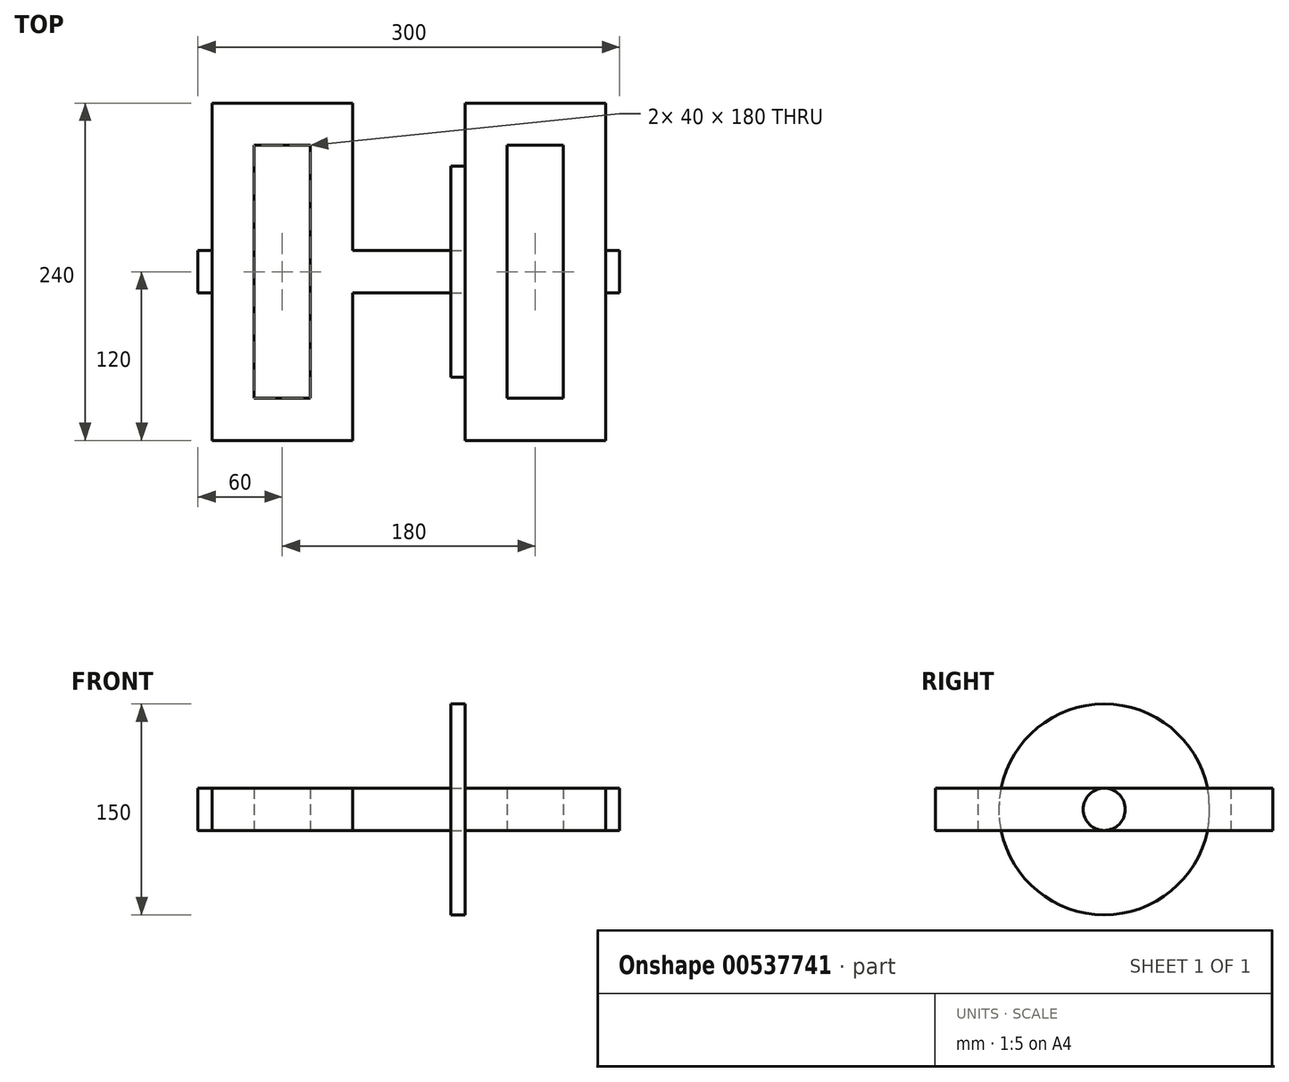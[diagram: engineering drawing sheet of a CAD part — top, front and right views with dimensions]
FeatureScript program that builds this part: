
annotation { "Feature Type Name" : "Feature", "Feature Type Description" : "" }
export const myFeature = defineFeature(function(context is Context, id is Id, definition is map)
    precondition{}
    {
        {
            var Q0;
            Q0=qCreatedBy(makeId("Top.planeOp"),FACE);
            var sketch = newSketch(context, id + "F0", { "sketchPlane" : qUnion([Q0])});
            skLineSegment(sketch, "E0.bottom", {"start": v(-150, 15) * mm, "end": v(-140, 15) * mm});
            skLineSegment(sketch, "E0.top", {"start": v(-150, -15) * mm, "end": v(-140, -15) * mm});
            skLineSegment(sketch, "E0.left", {"start": v(-150, 15) * mm, "end": v(-150, -15) * mm});
            skLineSegment(sketch, "E0.right", {"start": v(-140, 15) * mm, "end": v(-140, -15) * mm});
            skLineSegment(sketch, "E1.bottom", {"start": v(-140, 120) * mm, "end": v(-40, 120) * mm});
            skLineSegment(sketch, "E1.top", {"start": v(-140, -120) * mm, "end": v(-40, -120) * mm});
            skLineSegment(sketch, "E1.left", {"start": v(-140, 120) * mm, "end": v(-140, -120) * mm});
            skLineSegment(sketch, "E1.right", {"start": v(-40, 120) * mm, "end": v(-40, -120) * mm});
            skLineSegment(sketch, "E2.bottom", {"start": v(-40, 15) * mm, "end": v(40, 15) * mm});
            skLineSegment(sketch, "E2.top", {"start": v(-40, -15) * mm, "end": v(40, -15) * mm});
            skLineSegment(sketch, "E2.left", {"start": v(-40, 15) * mm, "end": v(-40, -15) * mm});
            skLineSegment(sketch, "E2.right", {"start": v(40, 15) * mm, "end": v(40, -15) * mm});
            skLineSegment(sketch, "E3.bottom", {"start": v(40, 120) * mm, "end": v(140, 120) * mm});
            skLineSegment(sketch, "E3.top", {"start": v(40, -120) * mm, "end": v(140, -120) * mm});
            skLineSegment(sketch, "E3.left", {"start": v(40, 120) * mm, "end": v(40, -120) * mm});
            skLineSegment(sketch, "E3.right", {"start": v(140, 120) * mm, "end": v(140, -120) * mm});
            skLineSegment(sketch, "E4.bottom", {"start": v(140, 15) * mm, "end": v(150, 15) * mm});
            skLineSegment(sketch, "E4.top", {"start": v(140, -15) * mm, "end": v(150, -15) * mm});
            skLineSegment(sketch, "E4.left", {"start": v(140, 15) * mm, "end": v(140, -15) * mm});
            skLineSegment(sketch, "E4.right", {"start": v(150, 15) * mm, "end": v(150, -15) * mm});
            skLineSegment(sketch, "E5.bottom", {"start": v(-110, 90) * mm, "end": v(-70, 90) * mm});
            skLineSegment(sketch, "E5.top", {"start": v(-110, -90) * mm, "end": v(-70, -90) * mm});
            skLineSegment(sketch, "E5.left", {"start": v(-110, 90) * mm, "end": v(-110, -90) * mm});
            skLineSegment(sketch, "E5.right", {"start": v(-70, 90) * mm, "end": v(-70, -90) * mm});
            skPoint(sketch, "E6.oppositeSnap0", {"position": v(-90, -90) * mm});
            skLineSegment(sketch, "E6.bottom", {"start": v(70, 90) * mm, "end": v(110, 90) * mm});
            skLineSegment(sketch, "E6.top", {"start": v(70, -90) * mm, "end": v(110, -90) * mm});
            skLineSegment(sketch, "E6.left", {"start": v(70, 90) * mm, "end": v(70, -90) * mm});
            skLineSegment(sketch, "E6.right", {"start": v(110, 90) * mm, "end": v(110, -90) * mm});
            skSolve(sketch);
        }
        {
            var Q0;
            {var subQ0=sQuery(id+"F0.wireOp",EDGE,"E0.bottom");Q0=makeQuery(id+"F0.imprint","IMPRINT",FACE,{"disambiguationData":[TD([[makeQuery(id+"F0.imprint","IMPRINT",EDGE,{"derivedFrom":subQ0}),-1.0]])]});}
            var Q1;
            {var subQ3=sQuery(id+"F0.wireOp",EDGE,"E1.bottom");Q1=makeQuery(id+"F0.imprint","IMPRINT",FACE,{"disambiguationData":[TD([[makeQuery(id+"F0.imprint","IMPRINT",EDGE,{"derivedFrom":subQ3}),-1.0]])]});}
            var Q2;
            {var subQ0=sQuery(id+"F0.wireOp",EDGE,"E2.bottom");Q2=makeQuery(id+"F0.imprint","IMPRINT",FACE,{"disambiguationData":[TD([[makeQuery(id+"F0.imprint","IMPRINT",EDGE,{"derivedFrom":subQ0}),-1.0]])]});}
            var Q3;
            {var subQ3=sQuery(id+"F0.wireOp",EDGE,"E3.bottom");Q3=makeQuery(id+"F0.imprint","IMPRINT",FACE,{"disambiguationData":[TD([[makeQuery(id+"F0.imprint","IMPRINT",EDGE,{"derivedFrom":subQ3}),-1.0]])]});}
            var Q4;
            Q4=makeQuery(id+"F0.imprint","IMPRINT",FACE,{"disambiguationData":[TD([[makeQuery(id+"F0.imprint","IMPRINT",EDGE,{"derivedFrom":sQuery(id+"F0.wireOp",EDGE,"E4.bottom")}),-1.0]])]});
            extrude(context, id + "F1", {"entities" : qUnion([Q0, Q1, Q2, Q3, Q4]), "endBound" : BoundingType.SYMMETRIC, "depth" : 30 * mm, "offsetDistance" : 25 * mm});
        }
        {
            var Q0;
            Q0=makeQuery(id+"F1.opExtrude","CAP_EDGE",EDGE,{"disambiguationData":[OSD([sQuery(id+"F0.wireOp",EDGE,"E0.top")])],"isStart":false});
            fillet(context, id + "F2", {"entities" : qUnion([Q0]), "radius" : 15 * mm, "tangentPropagation" : true, "allowEdgeOverflow" : false});
        }
        {
            var Q0;
            Q0=makeQuery(id+"F1.opExtrude","CAP_EDGE",EDGE,{"disambiguationData":[OSD([sQuery(id+"F0.wireOp",EDGE,"E0.top")])],"isStart":true});
            var Q1;
            Q1=makeQuery(id+"F1.opExtrude","CAP_EDGE",EDGE,{"disambiguationData":[OSD([sQuery(id+"F0.wireOp",EDGE,"E0.bottom")])],"isStart":true});
            var Q2;
            Q2=makeQuery(id+"F1.opExtrude","CAP_EDGE",EDGE,{"disambiguationData":[OSD([sQuery(id+"F0.wireOp",EDGE,"E0.bottom")])],"isStart":false});
            var Q3;
            Q3=makeQuery(id+"F1.opExtrude","CAP_EDGE",EDGE,{"disambiguationData":[OSD([sQuery(id+"F0.wireOp",EDGE,"E4.bottom")])],"isStart":true});
            var Q4;
            Q4=makeQuery(id+"F1.opExtrude","CAP_EDGE",EDGE,{"disambiguationData":[OSD([sQuery(id+"F0.wireOp",EDGE,"E4.bottom")])],"isStart":false});
            var Q5;
            Q5=makeQuery(id+"F1.opExtrude","CAP_EDGE",EDGE,{"disambiguationData":[OSD([sQuery(id+"F0.wireOp",EDGE,"E4.top")])],"isStart":false});
            var Q6;
            Q6=makeQuery(id+"F1.opExtrude","CAP_EDGE",EDGE,{"disambiguationData":[OSD([sQuery(id+"F0.wireOp",EDGE,"E4.top")])],"isStart":true});
            fillet(context, id + "F3", {"entities" : qUnion([Q0, Q1, Q2, Q3, Q4, Q5, Q6]), "radius" : 15 * mm, "tangentPropagation" : true, "allowEdgeOverflow" : false});
        }
        {
            var Q0;
            Q0=qCreatedBy(makeId("Right.planeOp"),FACE);
            var sketch = newSketch(context, id + "F4", { "sketchPlane" : qUnion([Q0])});
            skCircle(sketch, "E7", {"center": v(0, 0) * mm, "radius": 75 * mm});
            skSolve(sketch);
        }
        {
            var Q0;
            Q0 = qSketchRegion(id + "F4", true);
            var Q1;
            {var subQ0=sQuery(id+"F0.wireOp",EDGE,"E3.left");Q1=makeQuery(id+"F1.opExtrude","SWEPT_FACE",FACE,{"disambiguationData":[OSD([subQ0]),TDD([makeQuery(id+"F0.imprint","IMPRINT",EDGE,{"disambiguationData":[TD([[makeQuery(id+"F0.imprint","INTERSECT",VERTEX,{"derivedFrom":[sQuery(id+"F0.wireOp",EDGE,"E2.top"),subQ0]}),-1.0]])],"derivedFrom":subQ0})])]});}
            extrude(context, id + "F5", {"entities" : qUnion([Q0]), "endBound" : BoundingType.UP_TO_SURFACE, "depth" : 25 * mm, "endBoundEntityFace" : qUnion([Q1]), "offsetDistance" : 10 * mm, "hasSecondDirection" : true, "secondDirectionOppositeDirection" : false, "secondDirectionDepth" : 30 * mm, "hasSecondDirectionOffset" : true, "secondDirectionOffsetDistance" : 10 * mm});
        }
    });
